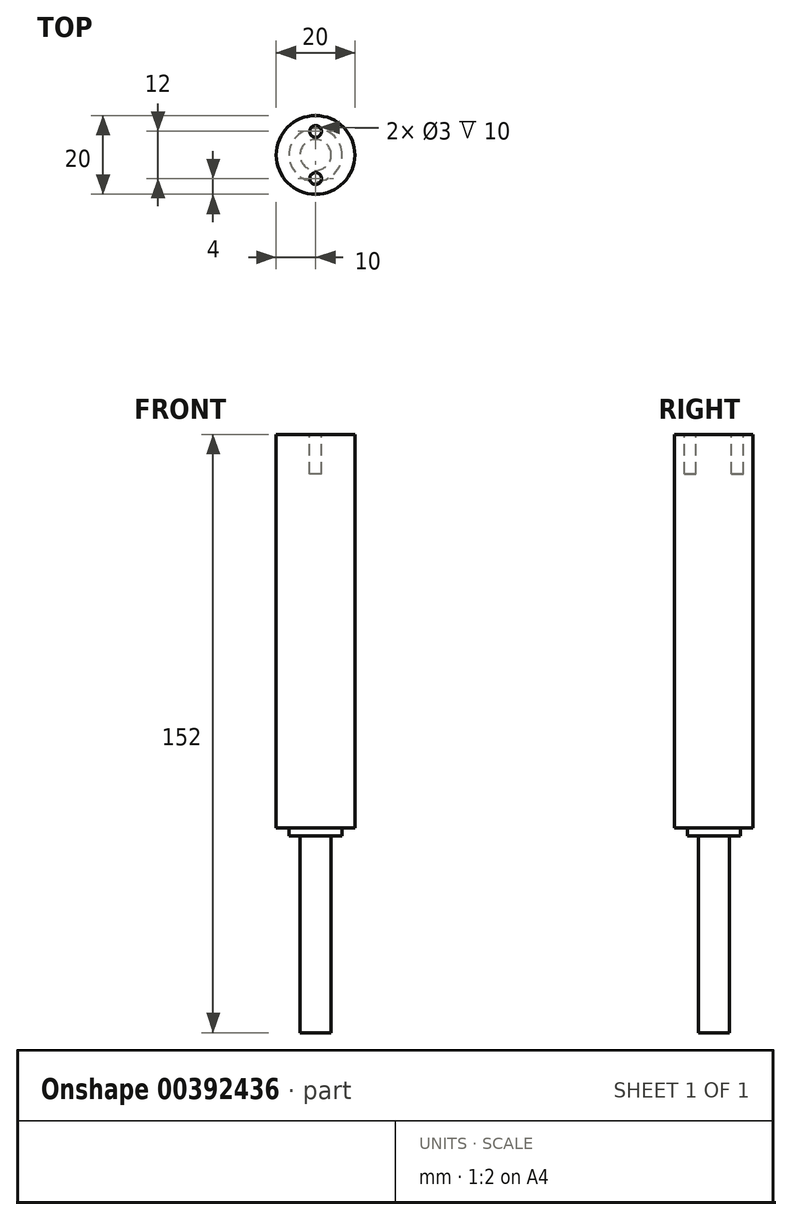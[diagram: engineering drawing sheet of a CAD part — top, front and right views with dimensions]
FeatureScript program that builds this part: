
annotation { "Feature Type Name" : "Feature", "Feature Type Description" : "" }
export const myFeature = defineFeature(function(context is Context, id is Id, definition is map)
    precondition{}
    {
        {
            var Q0;
            Q0=qCreatedBy(makeId("Top.planeOp"),FACE);
            var sketch = newSketch(context, id + "F0", { "sketchPlane" : qUnion([Q0])});
            skCircle(sketch, "E0", {"center": v(0, 0) * mm, "radius": 3.95 * mm});
            skSolve(sketch);
        }
        {
            var Q0;
            Q0=makeQuery(id+"F0.imprint","IMPRINT",FACE,{"disambiguationData":[TD([[makeQuery(id+"F0.imprint","IMPRINT",EDGE,{"derivedFrom":sQuery(id+"F0.wireOp",EDGE,"E0")}),1.0]])]});
            extrude(context, id + "F1", {"entities" : qUnion([Q0]), "depth" : 50 * mm});
        }
        {
            var Q0;
            Q0=makeQuery(id+"F1.opExtrude","CAP_FACE",FACE,{"disambiguationData":[OSD([sQuery(id+"F0.wireOp",EDGE,"E0")])],"isStart":false});
            var sketch = newSketch(context, id + "F2", { "sketchPlane" : qUnion([Q0])});
            skCircle(sketch, "E1", {"center": v(0, 0) * mm, "radius": 6.75 * mm});
            skSolve(sketch);
        }
        {
            var Q0;
            Q0=makeQuery(id+"F2.imprint","IMPRINT",FACE,{"disambiguationData":[TD([[makeQuery(id+"F2.imprint","IMPRINT",EDGE,{"derivedFrom":sQuery(id+"F2.wireOp",EDGE,"E1")}),1.0]])]});
            var Q1;
            Q1=makeQuery(id+"F2.imprint","IMPRINT",FACE,{"disambiguationData":[TD([[makeQuery(id+"F2.imprint","IMPRINT",EDGE,{"derivedFrom":makeQuery(id+"F1.opExtrude","CAP_EDGE",EDGE,{"disambiguationData":[OSD([sQuery(id+"F0.wireOp",EDGE,"E0")])],"isStart":false})}),1.0]])]});
            extrude(context, id + "F3", {"entities" : qUnion([Q0, Q1]), "operationType" : NewBodyOperationType.ADD, "depth" : 2 * mm});
        }
        {
            var Q0;
            Q0=makeQuery(id+"F3.opExtrude","CAP_FACE",FACE,{"disambiguationData":[OSD([sQuery(id+"F2.wireOp",EDGE,"E1")])],"isStart":false});
            var sketch = newSketch(context, id + "F4", { "sketchPlane" : qUnion([Q0])});
            skCircle(sketch, "E2", {"center": v(0, 0) * mm, "radius": 10 * mm});
            skSolve(sketch);
        }
        {
            var Q0;
            Q0=makeQuery(id+"F4.imprint","IMPRINT",FACE,{"disambiguationData":[TD([[makeQuery(id+"F4.imprint","IMPRINT",EDGE,{"derivedFrom":sQuery(id+"F4.wireOp",EDGE,"E2")}),1.0]])]});
            var Q1;
            Q1=makeQuery(id+"F4.imprint","IMPRINT",FACE,{"disambiguationData":[TD([[makeQuery(id+"F4.imprint","IMPRINT",EDGE,{"derivedFrom":makeQuery(id+"F1.opExtrude","CAP_EDGE",EDGE,{"disambiguationData":[OSD([sQuery(id+"F0.wireOp",EDGE,"E0")])],"isStart":false})}),1.0]])]});
            var Q2;
            Q2=makeQuery(id+"F4.imprint","IMPRINT",FACE,{"disambiguationData":[TD([[makeQuery(id+"F4.imprint","IMPRINT",EDGE,{"derivedFrom":makeQuery(id+"F3.opExtrude","CAP_EDGE",EDGE,{"disambiguationData":[OSD([sQuery(id+"F2.wireOp",EDGE,"E1")])],"isStart":false})}),1.0]])]});
            extrude(context, id + "F5", {"entities" : qUnion([Q0, Q1, Q2]), "operationType" : NewBodyOperationType.ADD, "depth" : 100 * mm});
        }
        {
            var Q0;
            Q0=makeQuery(id+"F5.opExtrude","CAP_FACE",FACE,{"disambiguationData":[OSD([sQuery(id+"F4.wireOp",EDGE,"E2")])],"isStart":false});
            var sketch = newSketch(context, id + "F6", { "sketchPlane" : qUnion([Q0])});
            skCircle(sketch, "E3", {"center": v(0, -6) * mm, "radius": 1.5 * mm});
            skCircle(sketch, "E4", {"center": v(0, 6) * mm, "radius": 1.5 * mm});
            skSolve(sketch);
        }
        {
            var Q0;
            Q0=makeQuery(id+"F6.imprint","IMPRINT",FACE,{"disambiguationData":[TD([[makeQuery(id+"F6.imprint","IMPRINT",EDGE,{"derivedFrom":sQuery(id+"F6.wireOp",EDGE,"E4")}),1.0]])]});
            var Q1;
            Q1=makeQuery(id+"F6.imprint","IMPRINT",FACE,{"disambiguationData":[TD([[makeQuery(id+"F6.imprint","IMPRINT",EDGE,{"derivedFrom":sQuery(id+"F6.wireOp",EDGE,"E3")}),1.0]])]});
            extrude(context, id + "F7", {"entities" : qUnion([Q0, Q1]), "operationType" : NewBodyOperationType.REMOVE, "oppositeDirection" : true, "depth" : 10 * mm});
        }
    });
